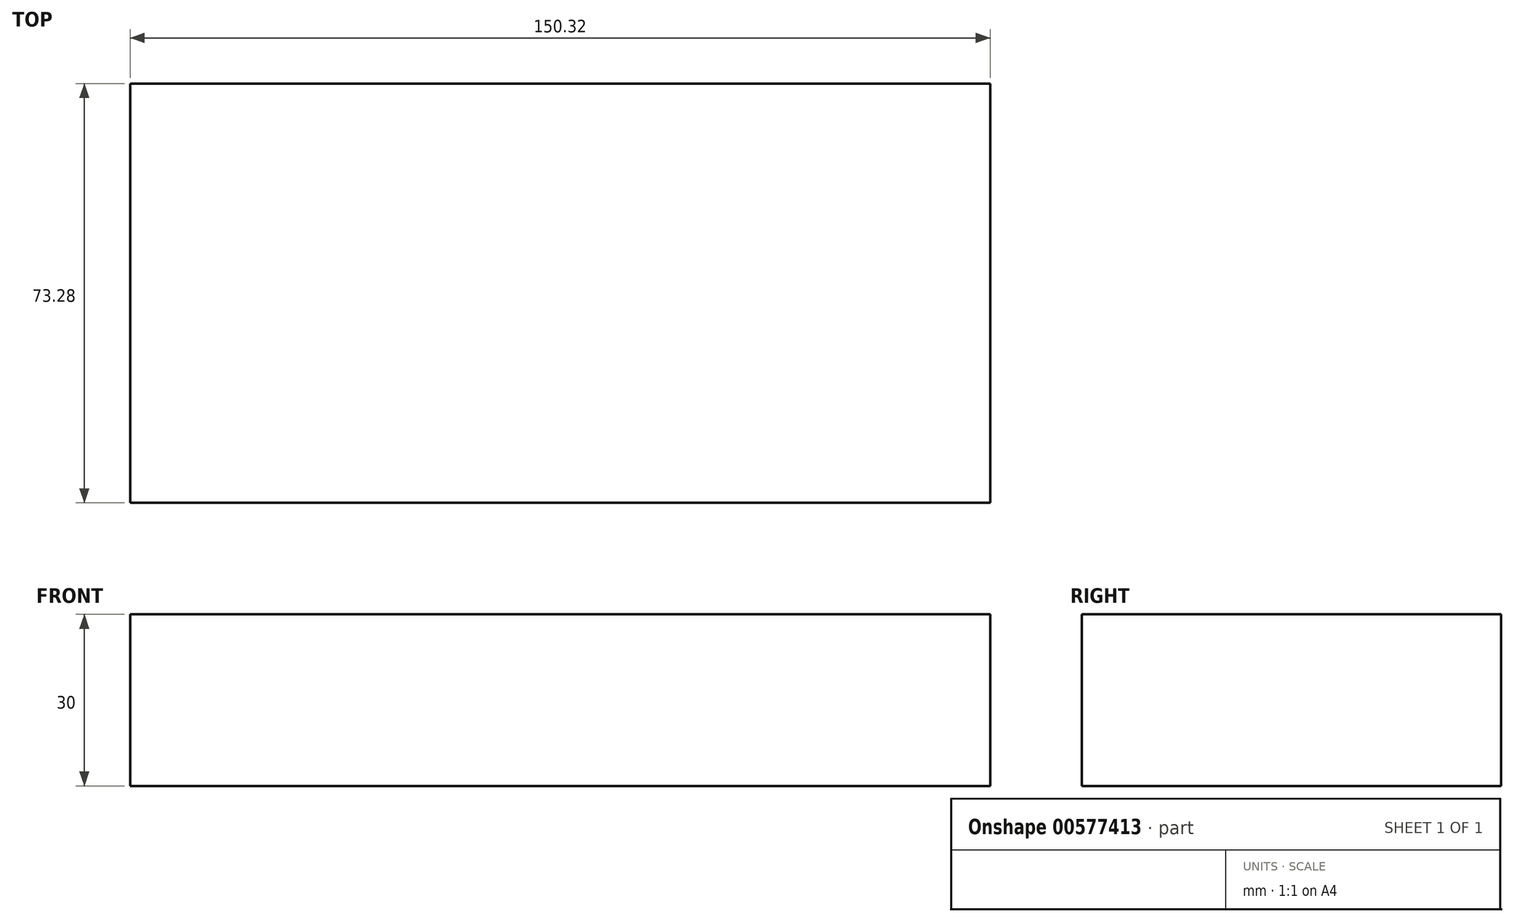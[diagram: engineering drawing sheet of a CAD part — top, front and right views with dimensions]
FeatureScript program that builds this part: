
annotation { "Feature Type Name" : "Feature", "Feature Type Description" : "" }
export const myFeature = defineFeature(function(context is Context, id is Id, definition is map)
    precondition{}
    {
        {
            var Q0;
            Q0=qCreatedBy(makeId("Top.planeOp"),FACE);
            var sketch = newSketch(context, id + "F0", { "sketchPlane" : qUnion([Q0])});
            skLineSegment(sketch, "E0.bottom", {"start": v(75.16, -36.64) * mm, "end": v(-75.16, -36.64) * mm});
            skLineSegment(sketch, "E0.top", {"start": v(75.16, 36.64) * mm, "end": v(-75.16, 36.64) * mm});
            skLineSegment(sketch, "E0.left", {"start": v(75.16, -36.64) * mm, "end": v(75.16, 36.64) * mm});
            skLineSegment(sketch, "E0.right", {"start": v(-75.16, -36.64) * mm, "end": v(-75.16, 36.64) * mm});
            skPoint(sketch, "E0.middle", {"position": v(0, 0) * mm});
            skSolve(sketch);
        }
        {
            var Q0;
            Q0 = qSketchRegion(id + "F0", true);
            extrude(context, id + "F1", {"entities" : qUnion([Q0]), "depth" : 30 * mm, "offsetDistance" : 25 * mm});
        }
    });
